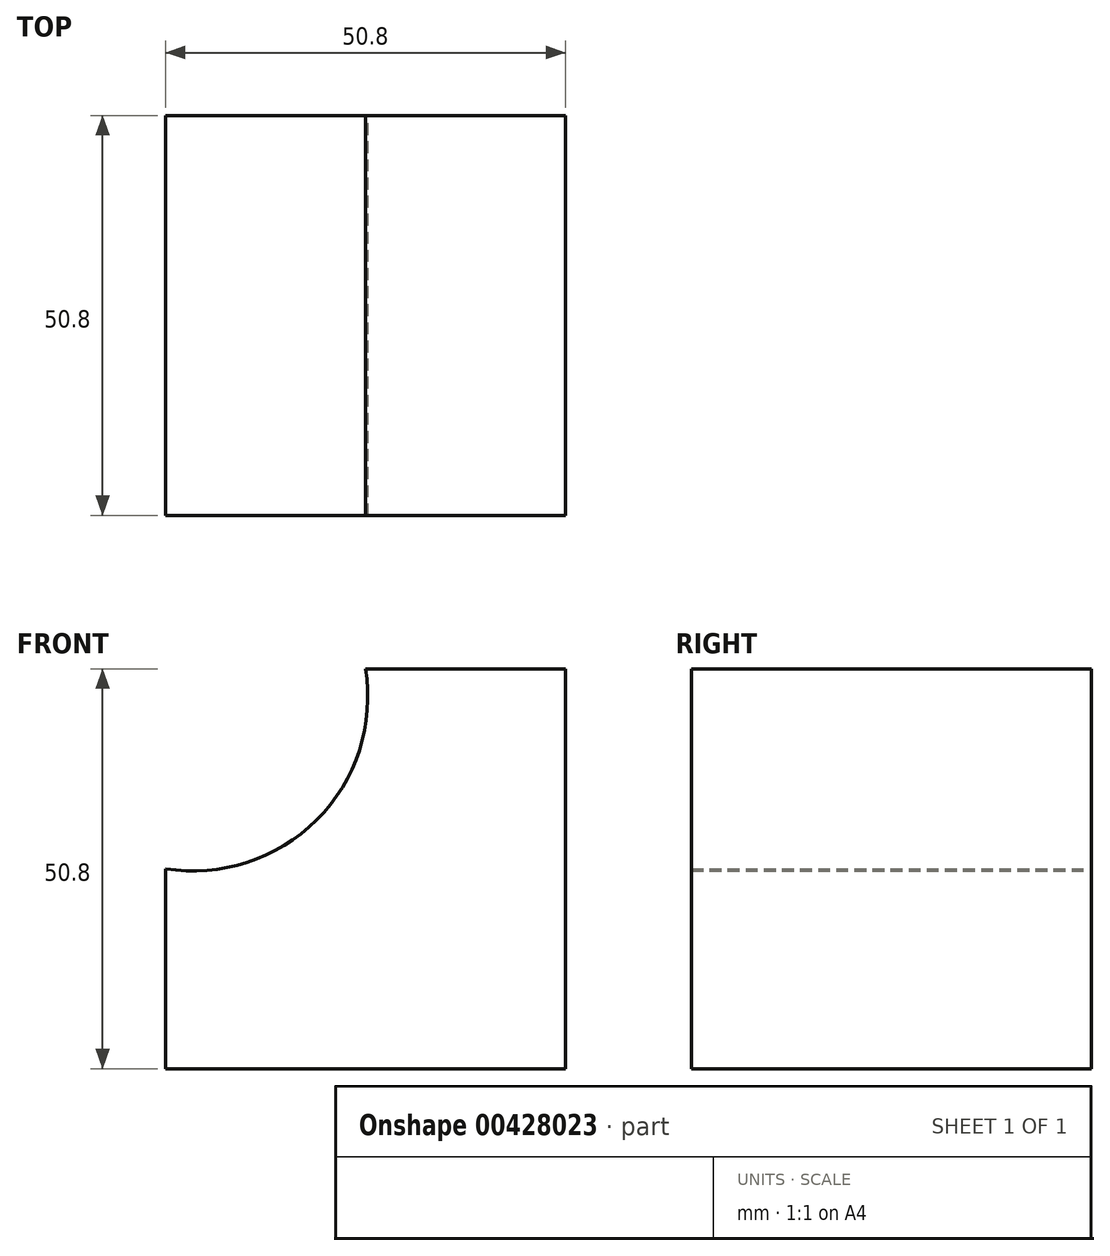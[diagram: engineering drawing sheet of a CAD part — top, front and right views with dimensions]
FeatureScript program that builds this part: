
annotation { "Feature Type Name" : "Feature", "Feature Type Description" : "" }
export const myFeature = defineFeature(function(context is Context, id is Id, definition is map)
    precondition{}
    {
        {
            var Q0;
            Q0=qCreatedBy(makeId("Front.planeOp"),FACE);
            var sketch = newSketch(context, id + "F0", { "sketchPlane" : qUnion([Q0])});
            skLineSegment(sketch, "E0", {"start": v(0, 0) * mm, "end": v(0, 50.8) * mm});
            skLineSegment(sketch, "E1", {"start": v(0, 0) * mm, "end": v(-50.8, 0) * mm});
            skLineSegment(sketch, "E2", {"start": v(-50.8, 0) * mm, "end": v(-50.8, 25.4) * mm});
            skLineSegment(sketch, "E3", {"start": v(0, 50.8) * mm, "end": v(-25.4, 50.8) * mm});
            skArc(sketch, "E4", {"start": v(-50.8, 25.4) * mm, "mid": v(-31.6, 31.6) * mm, "end": v(-25.4, 50.8) * mm});
            skSolve(sketch);
        }
        {
            var Q0;
            Q0 = qSketchRegion(id + "F0", true);
            extrude(context, id + "F1", {"entities" : qUnion([Q0]), "depth" : 50.8 * mm});
        }
    });
